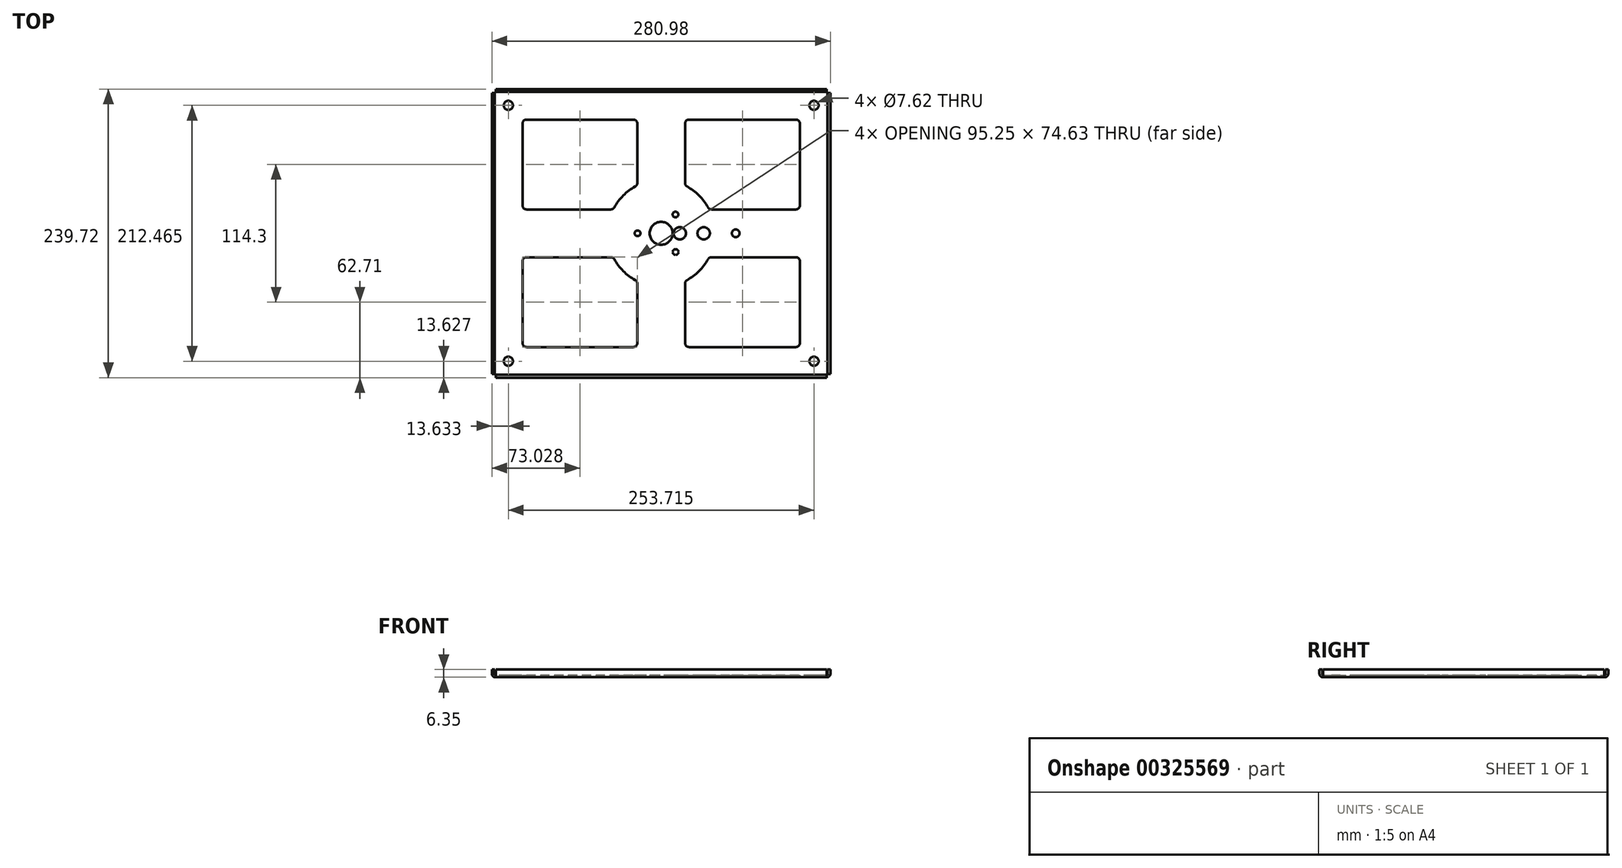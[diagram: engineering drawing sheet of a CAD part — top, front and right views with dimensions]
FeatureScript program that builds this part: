
annotation { "Feature Type Name" : "Feature", "Feature Type Description" : "" }
export const myFeature = defineFeature(function(context is Context, id is Id, definition is map)
    precondition{}
    {
        {
            var Q0;
            Q0=qCreatedBy(makeId("Top.planeOp"),FACE);
            var sketch = newSketch(context, id + "F0", { "sketchPlane" : qUnion([Q0])});
            skArc(sketch, "E0", {"start": v(-21.48, 38.92) * mm, "mid": v(-31.43, 31.43) * mm, "end": v(-38.92, 21.48) * mm});
            skLineSegment(sketch, "E1", {"start": v(-140.49, 116.69) * mm, "end": v(-140.49, -116.69) * mm});
            skLineSegment(sketch, "E2.0", {"start": v(-115.09, 91.29) * mm, "end": v(-115.09, 23.01) * mm});
            skLineSegment(sketch, "E3.0", {"start": v(-19.84, 91.29) * mm, "end": v(-19.84, 41.7) * mm});
            skLineSegment(sketch, "E4.0", {"start": v(19.84, 91.29) * mm, "end": v(19.84, 41.7) * mm});
            skLineSegment(sketch, "E5.0", {"start": v(115.09, 91.29) * mm, "end": v(115.09, 23.01) * mm});
            skLineSegment(sketch, "E6.0", {"start": v(140.49, 116.69) * mm, "end": v(140.49, -116.69) * mm});
            skLineSegment(sketch, "E7", {"start": v(-137.31, -119.86) * mm, "end": v(137.31, -119.86) * mm});
            skLineSegment(sketch, "E8.0", {"start": v(-111.91, -94.46) * mm, "end": v(-23.01, -94.46) * mm});
            skLineSegment(sketch, "E9.0", {"start": v(-111.91, -19.84) * mm, "end": v(-41.7, -19.84) * mm});
            skLineSegment(sketch, "E10.0", {"start": v(-111.91, 19.84) * mm, "end": v(-41.7, 19.84) * mm});
            skLineSegment(sketch, "E11.0", {"start": v(-111.91, 94.46) * mm, "end": v(-23.01, 94.46) * mm});
            skLineSegment(sketch, "E12.0", {"start": v(-137.31, 119.86) * mm, "end": v(137.31, 119.86) * mm});
            skLineSegment(sketch, "E13.trimOffspring", {"start": v(23.01, -94.46) * mm, "end": v(111.91, -94.46) * mm});
            skLineSegment(sketch, "E14.trimOffspring", {"start": v(-115.09, -23.01) * mm, "end": v(-115.09, -91.29) * mm});
            skLineSegment(sketch, "E15.trimOffspring", {"start": v(23.01, 94.46) * mm, "end": v(111.91, 94.46) * mm});
            skArc(sketch, "E16.trimOffspring", {"start": v(-38.92, -21.48) * mm, "mid": v(-31.43, -31.43) * mm, "end": v(-21.48, -38.92) * mm});
            skLineSegment(sketch, "E17.trimOffspring", {"start": v(41.7, 19.84) * mm, "end": v(111.91, 19.84) * mm});
            skArc(sketch, "E18.trimOffspring", {"start": v(38.92, 21.48) * mm, "mid": v(31.43, 31.43) * mm, "end": v(21.48, 38.92) * mm});
            skLineSegment(sketch, "E19.trimOffspring", {"start": v(41.7, -19.84) * mm, "end": v(111.91, -19.84) * mm});
            skLineSegment(sketch, "E20.trimOffspring", {"start": v(19.84, -41.7) * mm, "end": v(19.84, -91.29) * mm});
            skArc(sketch, "E21.trimOffspring", {"start": v(21.48, -38.92) * mm, "mid": v(31.43, -31.43) * mm, "end": v(38.92, -21.48) * mm});
            skLineSegment(sketch, "E22.trimOffspring", {"start": v(-19.84, -41.7) * mm, "end": v(-19.84, -91.29) * mm});
            skPoint(sketch, "E23.visualSharp", {"position": v(-115.09, 94.46) * mm});
            skArc(sketch, "E23.filletArc", {"start": v(-111.91, 94.46) * mm, "mid": v(-114.16, 93.53) * mm, "end": v(-115.09, 91.29) * mm});
            skPoint(sketch, "E24.visualSharp", {"position": v(-115.09, 19.84) * mm});
            skArc(sketch, "E24.filletArc", {"start": v(-115.09, 23.01) * mm, "mid": v(-114.16, 20.77) * mm, "end": v(-111.91, 19.84) * mm});
            skPoint(sketch, "E25.visualSharp", {"position": v(-39.78, 19.84) * mm});
            skArc(sketch, "E25.filletArc", {"start": v(-41.7, 19.84) * mm, "mid": v(-40.08, 20.28) * mm, "end": v(-38.92, 21.48) * mm});
            skPoint(sketch, "E26.visualSharp", {"position": v(-19.84, 39.78) * mm});
            skArc(sketch, "E26.filletArc", {"start": v(-21.48, 38.92) * mm, "mid": v(-20.28, 40.08) * mm, "end": v(-19.84, 41.7) * mm});
            skPoint(sketch, "E27.visualSharp", {"position": v(-19.84, 94.46) * mm});
            skArc(sketch, "E27.filletArc", {"start": v(-19.84, 91.29) * mm, "mid": v(-20.77, 93.53) * mm, "end": v(-23.01, 94.46) * mm});
            skPoint(sketch, "E28.visualSharp", {"position": v(19.84, 94.46) * mm});
            skArc(sketch, "E28.filletArc", {"start": v(23.01, 94.46) * mm, "mid": v(20.77, 93.53) * mm, "end": v(19.84, 91.29) * mm});
            skPoint(sketch, "E29.visualSharp", {"position": v(19.84, 39.78) * mm});
            skArc(sketch, "E29.filletArc", {"start": v(19.84, 41.7) * mm, "mid": v(20.28, 40.08) * mm, "end": v(21.48, 38.92) * mm});
            skPoint(sketch, "E30.visualSharp", {"position": v(39.78, 19.84) * mm});
            skArc(sketch, "E30.filletArc", {"start": v(38.92, 21.48) * mm, "mid": v(40.08, 20.28) * mm, "end": v(41.7, 19.84) * mm});
            skArc(sketch, "E31.filletArc", {"start": v(111.91, 19.84) * mm, "mid": v(114.16, 20.77) * mm, "end": v(115.09, 23.01) * mm});
            skPoint(sketch, "E32.visualSharp", {"position": v(115.09, 94.46) * mm});
            skArc(sketch, "E32.filletArc", {"start": v(115.09, 91.29) * mm, "mid": v(114.16, 93.53) * mm, "end": v(111.91, 94.46) * mm});
            skPoint(sketch, "E33.visualSharp", {"position": v(-39.78, -19.84) * mm});
            skArc(sketch, "E33.filletArc", {"start": v(-38.92, -21.48) * mm, "mid": v(-40.08, -20.28) * mm, "end": v(-41.7, -19.84) * mm});
            skPoint(sketch, "E34.visualSharp", {"position": v(-19.84, -39.78) * mm});
            skArc(sketch, "E34.filletArc", {"start": v(-19.84, -41.7) * mm, "mid": v(-20.28, -40.08) * mm, "end": v(-21.48, -38.92) * mm});
            skPoint(sketch, "E35.visualSharp", {"position": v(-19.84, -94.46) * mm});
            skArc(sketch, "E35.filletArc", {"start": v(-23.01, -94.46) * mm, "mid": v(-20.77, -93.53) * mm, "end": v(-19.84, -91.29) * mm});
            skPoint(sketch, "E36.visualSharp", {"position": v(-115.09, -94.46) * mm});
            skArc(sketch, "E36.filletArc", {"start": v(-115.09, -91.29) * mm, "mid": v(-114.16, -93.53) * mm, "end": v(-111.91, -94.46) * mm});
            skPoint(sketch, "E37.visualSharp", {"position": v(-115.09, -19.84) * mm});
            skArc(sketch, "E37.filletArc", {"start": v(-111.91, -19.84) * mm, "mid": v(-114.16, -20.77) * mm, "end": v(-115.09, -23.01) * mm});
            skPoint(sketch, "E38.visualSharp", {"position": v(19.84, -39.78) * mm});
            skArc(sketch, "E38.filletArc", {"start": v(21.48, -38.92) * mm, "mid": v(20.28, -40.08) * mm, "end": v(19.84, -41.7) * mm});
            skPoint(sketch, "E39.visualSharp", {"position": v(39.78, -19.84) * mm});
            skArc(sketch, "E39.filletArc", {"start": v(41.7, -19.84) * mm, "mid": v(40.08, -20.28) * mm, "end": v(38.92, -21.48) * mm});
            skPoint(sketch, "E40.visualSharp", {"position": v(19.84, -94.46) * mm});
            skArc(sketch, "E40.filletArc", {"start": v(19.84, -91.29) * mm, "mid": v(20.77, -93.53) * mm, "end": v(23.01, -94.46) * mm});
            skLineSegment(sketch, "E41", {"start": v(115.09, -91.29) * mm, "end": v(115.09, -23.01) * mm});
            skPoint(sketch, "E42.visualSharp", {"position": v(115.09, -94.46) * mm});
            skArc(sketch, "E42.filletArc", {"start": v(111.91, -94.46) * mm, "mid": v(114.16, -93.53) * mm, "end": v(115.09, -91.29) * mm});
            skPoint(sketch, "E43.visualSharp", {"position": v(115.09, -19.84) * mm});
            skArc(sketch, "E43.filletArc", {"start": v(115.09, -23.01) * mm, "mid": v(114.16, -20.77) * mm, "end": v(111.91, -19.84) * mm});
            skPoint(sketch, "E44.visualSharp", {"position": v(140.49, 119.86) * mm});
            skArc(sketch, "E44.filletArc", {"start": v(140.49, 116.69) * mm, "mid": v(139.56, 118.93) * mm, "end": v(137.31, 119.86) * mm});
            skPoint(sketch, "E45.visualSharp", {"position": v(140.49, -119.86) * mm});
            skArc(sketch, "E45.filletArc", {"start": v(137.31, -119.86) * mm, "mid": v(139.56, -118.93) * mm, "end": v(140.49, -116.69) * mm});
            skPoint(sketch, "E46.visualSharp", {"position": v(-140.49, -119.86) * mm});
            skArc(sketch, "E46.filletArc", {"start": v(-140.49, -116.69) * mm, "mid": v(-139.56, -118.93) * mm, "end": v(-137.31, -119.86) * mm});
            skPoint(sketch, "E47.visualSharp", {"position": v(-140.49, 119.86) * mm});
            skArc(sketch, "E47.filletArc", {"start": v(-137.31, 119.86) * mm, "mid": v(-139.56, 118.93) * mm, "end": v(-140.49, 116.69) * mm});
            skLineSegment(sketch, "E48", {"start": v(-139.56, -118.93) * mm, "end": v(-114.16, -93.53) * mm});
            skPoint(sketch, "E49", {"position": v(-126.86, -106.23) * mm});
            skCircle(sketch, "E50", {"center": v(-126.86, -106.23) * mm, "radius": 3.81 * mm});
            skLineSegment(sketch, "E51", {"start": v(-139.56, 118.93) * mm, "end": v(-114.16, 93.53) * mm});
            skPoint(sketch, "E52", {"position": v(-126.86, 106.23) * mm});
            skCircle(sketch, "E53", {"center": v(-126.86, 106.23) * mm, "radius": 3.81 * mm});
            skLineSegment(sketch, "E54", {"start": v(114.16, 93.53) * mm, "end": v(139.56, 118.93) * mm});
            skPoint(sketch, "E55", {"position": v(126.86, 106.23) * mm});
            skCircle(sketch, "E56", {"center": v(126.86, 106.23) * mm, "radius": 3.81 * mm});
            skLineSegment(sketch, "E57", {"start": v(114.16, -93.53) * mm, "end": v(139.56, -118.93) * mm});
            skPoint(sketch, "E58", {"position": v(126.86, -106.23) * mm});
            skCircle(sketch, "E59", {"center": v(126.86, -106.23) * mm, "radius": 3.81 * mm});
            skCircle(sketch, "E60", {"center": v(15.47, 0) * mm, "radius": 5.16 * mm});
            skLineSegment(sketch, "E61", {"start": v(0, 0) * mm, "end": v(-174.23, 0) * mm, "construction": true});
            skLineSegment(sketch, "E62", {"start": v(-174.23, 0) * mm, "end": v(-174.23, 0) * mm});
            skLineSegment(sketch, "E63", {"start": v(0, 0) * mm, "end": v(180.46, 0) * mm, "construction": true});
            skLineSegment(sketch, "E64", {"start": v(0, -149.74) * mm, "end": v(0, 151.2) * mm, "construction": true});
            skCircle(sketch, "E65", {"center": v(0, 0) * mm, "radius": 9.53 * mm});
            skCircle(sketch, "E66", {"center": v(35.31, 0) * mm, "radius": 5.16 * mm});
            skCircle(sketch, "E67", {"center": v(-19.56, 0) * mm, "radius": 2.38 * mm});
            skPoint(sketch, "E68", {"position": v(-31.43, 31.43) * mm});
            skPoint(sketch, "E69", {"position": v(-31.43, -31.43) * mm});
            skCircle(sketch, "E70", {"center": v(0, 0) * mm, "radius": 17.22 * mm});
            skCircle(sketch, "E71", {"center": v(11.9, 15.59) * mm, "radius": 2.39 * mm});
            skCircle(sketch, "E72", {"center": v(12, -15.56) * mm, "radius": 2.39 * mm});
            skLineSegment(sketch, "E73", {"start": v(9.53, 0) * mm, "end": v(9.53, 25.1) * mm, "construction": true});
            skLineSegment(sketch, "E74", {"start": v(9.53, 0) * mm, "end": v(9.53, -24.17) * mm, "construction": true});
            skCircle(sketch, "E75", {"center": v(61.91, 0) * mm, "radius": 3.18 * mm});
            skSolve(sketch);
        }
        {
            var Q0;
            Q0=makeQuery(id+"F0.imprint","IMPRINT",FACE,{"disambiguationData":[TD([[makeQuery(id+"F0.imprint","IMPRINT",EDGE,{"derivedFrom":sQuery(id+"F0.wireOp",EDGE,"E0")}),1.0]])]});
            var Q1;
            {var subQ14=sQuery(id+"F0.wireOp",EDGE,"E5.0");Q1=makeQuery(id+"F0.imprint","IMPRINT",FACE,{"disambiguationData":[TD([[makeQuery(id+"F0.imprint","IMPRINT",EDGE,{"derivedFrom":subQ14}),1.0]])]});}
            var Q2;
            Q2=makeQuery(id+"F0.imprint","IMPRINT",FACE,{"disambiguationData":[TD([[makeQuery(id+"F0.imprint","IMPRINT",EDGE,{"derivedFrom":sQuery(id+"F0.wireOp",EDGE,"E65")}),-1.0]])]});
            extrude(context, id + "F1", {"entities" : qUnion([Q0, Q1, Q2]), "depth" : 1.59 * mm});
        }
        {
            var Q0;
            Q0=qCreatedBy(makeId("Top.planeOp"),FACE);
            var sketch = newSketch(context, id + "F2", { "sketchPlane" : qUnion([Q0])});
            skLineSegment(sketch, "E76", {"start": v(-138.1, 116.68) * mm, "end": v(-138.1, -116.68) * mm});
            skLineSegment(sketch, "E77.0", {"start": v(-140.49, 116.68) * mm, "end": v(-140.49, -116.68) * mm});
            skLineSegment(sketch, "E78", {"start": v(138.1, 116.68) * mm, "end": v(138.1, -116.68) * mm});
            skLineSegment(sketch, "E79.0", {"start": v(140.49, 116.68) * mm, "end": v(140.49, -116.68) * mm});
            skLineSegment(sketch, "E80", {"start": v(-137.33, -117.48) * mm, "end": v(137.3, -117.48) * mm});
            skLineSegment(sketch, "E81.0", {"start": v(-137.33, 117.48) * mm, "end": v(137.3, 117.48) * mm});
            skLineSegment(sketch, "E82.0", {"start": v(-137.33, -119.86) * mm, "end": v(137.3, -119.86) * mm});
            skLineSegment(sketch, "E83", {"start": v(-137.33, 119.86) * mm, "end": v(-137.33, 117.48) * mm});
            skLineSegment(sketch, "E84", {"start": v(137.3, 119.86) * mm, "end": v(137.3, 117.48) * mm});
            skLineSegment(sketch, "E85", {"start": v(-140.49, 116.68) * mm, "end": v(-138.1, 116.68) * mm});
            skLineSegment(sketch, "E86", {"start": v(-140.49, -116.68) * mm, "end": v(-138.1, -116.68) * mm});
            skLineSegment(sketch, "E87.trimOffspring", {"start": v(-137.33, 119.86) * mm, "end": v(137.3, 119.86) * mm});
            skLineSegment(sketch, "E88.trimOffspring", {"start": v(137.3, -117.48) * mm, "end": v(137.3, -119.86) * mm});
            skLineSegment(sketch, "E89.trimOffspring", {"start": v(138.1, 116.68) * mm, "end": v(140.49, 116.68) * mm});
            skLineSegment(sketch, "E90.trimOffspring", {"start": v(-137.33, -117.48) * mm, "end": v(-137.33, -119.86) * mm});
            skLineSegment(sketch, "E91.trimOffspring", {"start": v(138.1, -116.68) * mm, "end": v(140.49, -116.68) * mm});
            skSolve(sketch);
        }
        {
            var Q0;
            Q0=makeQuery(id+"F2.imprint","IMPRINT",FACE,{"disambiguationData":[TD([[makeQuery(id+"F2.imprint","IMPRINT",EDGE,{"derivedFrom":sQuery(id+"F2.wireOp",EDGE,"E81.0")}),1.0]])]});
            var Q1;
            Q1=makeQuery(id+"F2.imprint","IMPRINT",FACE,{"disambiguationData":[TD([[makeQuery(id+"F2.imprint","IMPRINT",EDGE,{"derivedFrom":sQuery(id+"F2.wireOp",EDGE,"E78")}),1.0]])]});
            var Q2;
            Q2=makeQuery(id+"F2.imprint","IMPRINT",FACE,{"disambiguationData":[TD([[makeQuery(id+"F2.imprint","IMPRINT",EDGE,{"derivedFrom":sQuery(id+"F2.wireOp",EDGE,"E80")}),-1.0]])]});
            var Q3;
            Q3=makeQuery(id+"F2.imprint","IMPRINT",FACE,{"disambiguationData":[TD([[makeQuery(id+"F2.imprint","IMPRINT",EDGE,{"derivedFrom":sQuery(id+"F2.wireOp",EDGE,"E76")}),-1.0]])]});
            extrude(context, id + "F3", {"entities" : qUnion([Q0, Q1, Q2, Q3]), "operationType" : NewBodyOperationType.ADD, "depth" : 6.35 * mm});
        }
        {
            var Q0;
            Q0=makeQuery(id+"F3.boolean.opBoolean","INTERSECT",EDGE,{"derivedFrom":[makeQuery(id+"F1.opExtrude","CAP_FACE",FACE,{"disambiguationData":[OSD([sQuery(id+"F0.wireOp",EDGE,"E0"),sQuery(id+"F0.wireOp",EDGE,"E1"),sQuery(id+"F0.wireOp",EDGE,"E2.0"),sQuery(id+"F0.wireOp",EDGE,"E3.0"),sQuery(id+"F0.wireOp",EDGE,"E4.0"),sQuery(id+"F0.wireOp",EDGE,"E5.0"),sQuery(id+"F0.wireOp",EDGE,"E6.0"),sQuery(id+"F0.wireOp",EDGE,"E7"),sQuery(id+"F0.wireOp",EDGE,"E8.0"),sQuery(id+"F0.wireOp",EDGE,"E9.0"),sQuery(id+"F0.wireOp",EDGE,"E10.0"),sQuery(id+"F0.wireOp",EDGE,"E11.0"),sQuery(id+"F0.wireOp",EDGE,"E12.0"),sQuery(id+"F0.wireOp",EDGE,"E13.trimOffspring"),sQuery(id+"F0.wireOp",EDGE,"E14.trimOffspring"),sQuery(id+"F0.wireOp",EDGE,"E15.trimOffspring"),sQuery(id+"F0.wireOp",EDGE,"E16.trimOffspring"),sQuery(id+"F0.wireOp",EDGE,"E17.trimOffspring"),sQuery(id+"F0.wireOp",EDGE,"E18.trimOffspring"),sQuery(id+"F0.wireOp",EDGE,"E19.trimOffspring"),sQuery(id+"F0.wireOp",EDGE,"E20.trimOffspring"),sQuery(id+"F0.wireOp",EDGE,"E21.trimOffspring"),sQuery(id+"F0.wireOp",EDGE,"E22.trimOffspring"),sQuery(id+"F0.wireOp",EDGE,"E23.filletArc"),sQuery(id+"F0.wireOp",EDGE,"E24.filletArc"),sQuery(id+"F0.wireOp",EDGE,"E25.filletArc"),sQuery(id+"F0.wireOp",EDGE,"E26.filletArc"),sQuery(id+"F0.wireOp",EDGE,"E27.filletArc"),sQuery(id+"F0.wireOp",EDGE,"E28.filletArc"),sQuery(id+"F0.wireOp",EDGE,"E29.filletArc"),sQuery(id+"F0.wireOp",EDGE,"E30.filletArc"),sQuery(id+"F0.wireOp",EDGE,"E31.filletArc"),sQuery(id+"F0.wireOp",EDGE,"E32.filletArc"),sQuery(id+"F0.wireOp",EDGE,"E33.filletArc"),sQuery(id+"F0.wireOp",EDGE,"E34.filletArc"),sQuery(id+"F0.wireOp",EDGE,"E35.filletArc"),sQuery(id+"F0.wireOp",EDGE,"E36.filletArc"),sQuery(id+"F0.wireOp",EDGE,"E37.filletArc"),sQuery(id+"F0.wireOp",EDGE,"E38.filletArc"),sQuery(id+"F0.wireOp",EDGE,"E39.filletArc"),sQuery(id+"F0.wireOp",EDGE,"E40.filletArc"),sQuery(id+"F0.wireOp",EDGE,"E41"),sQuery(id+"F0.wireOp",EDGE,"E42.filletArc"),sQuery(id+"F0.wireOp",EDGE,"E43.filletArc"),sQuery(id+"F0.wireOp",EDGE,"E44.filletArc"),sQuery(id+"F0.wireOp",EDGE,"E45.filletArc"),sQuery(id+"F0.wireOp",EDGE,"E46.filletArc"),sQuery(id+"F0.wireOp",EDGE,"E47.filletArc"),sQuery(id+"F0.wireOp",EDGE,"E50"),sQuery(id+"F0.wireOp",EDGE,"E53"),sQuery(id+"F0.wireOp",EDGE,"E56"),sQuery(id+"F0.wireOp",EDGE,"E59"),sQuery(id+"F0.wireOp",EDGE,"E60"),sQuery(id+"F0.wireOp",EDGE,"4c565e8e-d8a4-4b50-a715-5eb734d49097")])],"isStart":false}),makeQuery(id+"F3.opExtrude","SWEPT_FACE",FACE,{"disambiguationData":[OSD([sQuery(id+"F2.wireOp",EDGE,"E81.0")])]})]});
            var Q1;
            Q1=makeQuery(id+"F3.boolean.opBoolean","INTERSECT",EDGE,{"derivedFrom":[makeQuery(id+"F1.opExtrude","CAP_FACE",FACE,{"disambiguationData":[OSD([sQuery(id+"F0.wireOp",EDGE,"E0"),sQuery(id+"F0.wireOp",EDGE,"E1"),sQuery(id+"F0.wireOp",EDGE,"E2.0"),sQuery(id+"F0.wireOp",EDGE,"E3.0"),sQuery(id+"F0.wireOp",EDGE,"E4.0"),sQuery(id+"F0.wireOp",EDGE,"E5.0"),sQuery(id+"F0.wireOp",EDGE,"E6.0"),sQuery(id+"F0.wireOp",EDGE,"E7"),sQuery(id+"F0.wireOp",EDGE,"E8.0"),sQuery(id+"F0.wireOp",EDGE,"E9.0"),sQuery(id+"F0.wireOp",EDGE,"E10.0"),sQuery(id+"F0.wireOp",EDGE,"E11.0"),sQuery(id+"F0.wireOp",EDGE,"E12.0"),sQuery(id+"F0.wireOp",EDGE,"E13.trimOffspring"),sQuery(id+"F0.wireOp",EDGE,"E14.trimOffspring"),sQuery(id+"F0.wireOp",EDGE,"E15.trimOffspring"),sQuery(id+"F0.wireOp",EDGE,"E16.trimOffspring"),sQuery(id+"F0.wireOp",EDGE,"E17.trimOffspring"),sQuery(id+"F0.wireOp",EDGE,"E18.trimOffspring"),sQuery(id+"F0.wireOp",EDGE,"E19.trimOffspring"),sQuery(id+"F0.wireOp",EDGE,"E20.trimOffspring"),sQuery(id+"F0.wireOp",EDGE,"E21.trimOffspring"),sQuery(id+"F0.wireOp",EDGE,"E22.trimOffspring"),sQuery(id+"F0.wireOp",EDGE,"E23.filletArc"),sQuery(id+"F0.wireOp",EDGE,"E24.filletArc"),sQuery(id+"F0.wireOp",EDGE,"E25.filletArc"),sQuery(id+"F0.wireOp",EDGE,"E26.filletArc"),sQuery(id+"F0.wireOp",EDGE,"E27.filletArc"),sQuery(id+"F0.wireOp",EDGE,"E28.filletArc"),sQuery(id+"F0.wireOp",EDGE,"E29.filletArc"),sQuery(id+"F0.wireOp",EDGE,"E30.filletArc"),sQuery(id+"F0.wireOp",EDGE,"E31.filletArc"),sQuery(id+"F0.wireOp",EDGE,"E32.filletArc"),sQuery(id+"F0.wireOp",EDGE,"E33.filletArc"),sQuery(id+"F0.wireOp",EDGE,"E34.filletArc"),sQuery(id+"F0.wireOp",EDGE,"E35.filletArc"),sQuery(id+"F0.wireOp",EDGE,"E36.filletArc"),sQuery(id+"F0.wireOp",EDGE,"E37.filletArc"),sQuery(id+"F0.wireOp",EDGE,"E38.filletArc"),sQuery(id+"F0.wireOp",EDGE,"E39.filletArc"),sQuery(id+"F0.wireOp",EDGE,"E40.filletArc"),sQuery(id+"F0.wireOp",EDGE,"E41"),sQuery(id+"F0.wireOp",EDGE,"E42.filletArc"),sQuery(id+"F0.wireOp",EDGE,"E43.filletArc"),sQuery(id+"F0.wireOp",EDGE,"E44.filletArc"),sQuery(id+"F0.wireOp",EDGE,"E45.filletArc"),sQuery(id+"F0.wireOp",EDGE,"E46.filletArc"),sQuery(id+"F0.wireOp",EDGE,"E47.filletArc"),sQuery(id+"F0.wireOp",EDGE,"E50"),sQuery(id+"F0.wireOp",EDGE,"E53"),sQuery(id+"F0.wireOp",EDGE,"E56"),sQuery(id+"F0.wireOp",EDGE,"E59"),sQuery(id+"F0.wireOp",EDGE,"E60"),sQuery(id+"F0.wireOp",EDGE,"4c565e8e-d8a4-4b50-a715-5eb734d49097")])],"isStart":false}),makeQuery(id+"F3.opExtrude","SWEPT_FACE",FACE,{"disambiguationData":[OSD([sQuery(id+"F2.wireOp",EDGE,"E78")])]})]});
            var Q2;
            Q2=makeQuery(id+"F3.boolean.opBoolean","INTERSECT",EDGE,{"derivedFrom":[makeQuery(id+"F1.opExtrude","CAP_FACE",FACE,{"disambiguationData":[OSD([sQuery(id+"F0.wireOp",EDGE,"E0"),sQuery(id+"F0.wireOp",EDGE,"E1"),sQuery(id+"F0.wireOp",EDGE,"E2.0"),sQuery(id+"F0.wireOp",EDGE,"E3.0"),sQuery(id+"F0.wireOp",EDGE,"E4.0"),sQuery(id+"F0.wireOp",EDGE,"E5.0"),sQuery(id+"F0.wireOp",EDGE,"E6.0"),sQuery(id+"F0.wireOp",EDGE,"E7"),sQuery(id+"F0.wireOp",EDGE,"E8.0"),sQuery(id+"F0.wireOp",EDGE,"E9.0"),sQuery(id+"F0.wireOp",EDGE,"E10.0"),sQuery(id+"F0.wireOp",EDGE,"E11.0"),sQuery(id+"F0.wireOp",EDGE,"E12.0"),sQuery(id+"F0.wireOp",EDGE,"E13.trimOffspring"),sQuery(id+"F0.wireOp",EDGE,"E14.trimOffspring"),sQuery(id+"F0.wireOp",EDGE,"E15.trimOffspring"),sQuery(id+"F0.wireOp",EDGE,"E16.trimOffspring"),sQuery(id+"F0.wireOp",EDGE,"E17.trimOffspring"),sQuery(id+"F0.wireOp",EDGE,"E18.trimOffspring"),sQuery(id+"F0.wireOp",EDGE,"E19.trimOffspring"),sQuery(id+"F0.wireOp",EDGE,"E20.trimOffspring"),sQuery(id+"F0.wireOp",EDGE,"E21.trimOffspring"),sQuery(id+"F0.wireOp",EDGE,"E22.trimOffspring"),sQuery(id+"F0.wireOp",EDGE,"E23.filletArc"),sQuery(id+"F0.wireOp",EDGE,"E24.filletArc"),sQuery(id+"F0.wireOp",EDGE,"E25.filletArc"),sQuery(id+"F0.wireOp",EDGE,"E26.filletArc"),sQuery(id+"F0.wireOp",EDGE,"E27.filletArc"),sQuery(id+"F0.wireOp",EDGE,"E28.filletArc"),sQuery(id+"F0.wireOp",EDGE,"E29.filletArc"),sQuery(id+"F0.wireOp",EDGE,"E30.filletArc"),sQuery(id+"F0.wireOp",EDGE,"E31.filletArc"),sQuery(id+"F0.wireOp",EDGE,"E32.filletArc"),sQuery(id+"F0.wireOp",EDGE,"E33.filletArc"),sQuery(id+"F0.wireOp",EDGE,"E34.filletArc"),sQuery(id+"F0.wireOp",EDGE,"E35.filletArc"),sQuery(id+"F0.wireOp",EDGE,"E36.filletArc"),sQuery(id+"F0.wireOp",EDGE,"E37.filletArc"),sQuery(id+"F0.wireOp",EDGE,"E38.filletArc"),sQuery(id+"F0.wireOp",EDGE,"E39.filletArc"),sQuery(id+"F0.wireOp",EDGE,"E40.filletArc"),sQuery(id+"F0.wireOp",EDGE,"E41"),sQuery(id+"F0.wireOp",EDGE,"E42.filletArc"),sQuery(id+"F0.wireOp",EDGE,"E43.filletArc"),sQuery(id+"F0.wireOp",EDGE,"E44.filletArc"),sQuery(id+"F0.wireOp",EDGE,"E45.filletArc"),sQuery(id+"F0.wireOp",EDGE,"E46.filletArc"),sQuery(id+"F0.wireOp",EDGE,"E47.filletArc"),sQuery(id+"F0.wireOp",EDGE,"E50"),sQuery(id+"F0.wireOp",EDGE,"E53"),sQuery(id+"F0.wireOp",EDGE,"E56"),sQuery(id+"F0.wireOp",EDGE,"E59"),sQuery(id+"F0.wireOp",EDGE,"E60"),sQuery(id+"F0.wireOp",EDGE,"4c565e8e-d8a4-4b50-a715-5eb734d49097")])],"isStart":false}),makeQuery(id+"F3.opExtrude","SWEPT_FACE",FACE,{"disambiguationData":[OSD([sQuery(id+"F2.wireOp",EDGE,"E80")])]})]});
            var Q3;
            Q3=makeQuery(id+"F3.boolean.opBoolean","INTERSECT",EDGE,{"derivedFrom":[makeQuery(id+"F1.opExtrude","CAP_FACE",FACE,{"disambiguationData":[OSD([sQuery(id+"F0.wireOp",EDGE,"E0"),sQuery(id+"F0.wireOp",EDGE,"E1"),sQuery(id+"F0.wireOp",EDGE,"E2.0"),sQuery(id+"F0.wireOp",EDGE,"E3.0"),sQuery(id+"F0.wireOp",EDGE,"E4.0"),sQuery(id+"F0.wireOp",EDGE,"E5.0"),sQuery(id+"F0.wireOp",EDGE,"E6.0"),sQuery(id+"F0.wireOp",EDGE,"E7"),sQuery(id+"F0.wireOp",EDGE,"E8.0"),sQuery(id+"F0.wireOp",EDGE,"E9.0"),sQuery(id+"F0.wireOp",EDGE,"E10.0"),sQuery(id+"F0.wireOp",EDGE,"E11.0"),sQuery(id+"F0.wireOp",EDGE,"E12.0"),sQuery(id+"F0.wireOp",EDGE,"E13.trimOffspring"),sQuery(id+"F0.wireOp",EDGE,"E14.trimOffspring"),sQuery(id+"F0.wireOp",EDGE,"E15.trimOffspring"),sQuery(id+"F0.wireOp",EDGE,"E16.trimOffspring"),sQuery(id+"F0.wireOp",EDGE,"E17.trimOffspring"),sQuery(id+"F0.wireOp",EDGE,"E18.trimOffspring"),sQuery(id+"F0.wireOp",EDGE,"E19.trimOffspring"),sQuery(id+"F0.wireOp",EDGE,"E20.trimOffspring"),sQuery(id+"F0.wireOp",EDGE,"E21.trimOffspring"),sQuery(id+"F0.wireOp",EDGE,"E22.trimOffspring"),sQuery(id+"F0.wireOp",EDGE,"E23.filletArc"),sQuery(id+"F0.wireOp",EDGE,"E24.filletArc"),sQuery(id+"F0.wireOp",EDGE,"E25.filletArc"),sQuery(id+"F0.wireOp",EDGE,"E26.filletArc"),sQuery(id+"F0.wireOp",EDGE,"E27.filletArc"),sQuery(id+"F0.wireOp",EDGE,"E28.filletArc"),sQuery(id+"F0.wireOp",EDGE,"E29.filletArc"),sQuery(id+"F0.wireOp",EDGE,"E30.filletArc"),sQuery(id+"F0.wireOp",EDGE,"E31.filletArc"),sQuery(id+"F0.wireOp",EDGE,"E32.filletArc"),sQuery(id+"F0.wireOp",EDGE,"E33.filletArc"),sQuery(id+"F0.wireOp",EDGE,"E34.filletArc"),sQuery(id+"F0.wireOp",EDGE,"E35.filletArc"),sQuery(id+"F0.wireOp",EDGE,"E36.filletArc"),sQuery(id+"F0.wireOp",EDGE,"E37.filletArc"),sQuery(id+"F0.wireOp",EDGE,"E38.filletArc"),sQuery(id+"F0.wireOp",EDGE,"E39.filletArc"),sQuery(id+"F0.wireOp",EDGE,"E40.filletArc"),sQuery(id+"F0.wireOp",EDGE,"E41"),sQuery(id+"F0.wireOp",EDGE,"E42.filletArc"),sQuery(id+"F0.wireOp",EDGE,"E43.filletArc"),sQuery(id+"F0.wireOp",EDGE,"E44.filletArc"),sQuery(id+"F0.wireOp",EDGE,"E45.filletArc"),sQuery(id+"F0.wireOp",EDGE,"E46.filletArc"),sQuery(id+"F0.wireOp",EDGE,"E47.filletArc"),sQuery(id+"F0.wireOp",EDGE,"E50"),sQuery(id+"F0.wireOp",EDGE,"E53"),sQuery(id+"F0.wireOp",EDGE,"E56"),sQuery(id+"F0.wireOp",EDGE,"E59"),sQuery(id+"F0.wireOp",EDGE,"E60"),sQuery(id+"F0.wireOp",EDGE,"4c565e8e-d8a4-4b50-a715-5eb734d49097")])],"isStart":false}),makeQuery(id+"F3.opExtrude","SWEPT_FACE",FACE,{"disambiguationData":[OSD([sQuery(id+"F2.wireOp",EDGE,"E76")])]})]});
            fillet(context, id + "F4", {"entities" : qUnion([Q0, Q1, Q2, Q3]), "radius" : 0.76 * mm, "tangentPropagation" : true, "allowEdgeOverflow" : false});
        }
        {
            var Q0;
            Q0=qCreatedBy(makeId("Top.planeOp"),FACE);
            var sketch = newSketch(context, id + "F5", { "sketchPlane" : qUnion([Q0])});
            skLineSegment(sketch, "E92.bottom", {"start": v(-141.66, 120.91) * mm, "end": v(-137.32, 120.91) * mm});
            skLineSegment(sketch, "E92.top", {"start": v(-141.66, 116.68) * mm, "end": v(-137.32, 116.68) * mm});
            skLineSegment(sketch, "E92.left", {"start": v(-141.66, 120.91) * mm, "end": v(-141.66, 116.68) * mm});
            skLineSegment(sketch, "E92.right", {"start": v(-137.32, 120.91) * mm, "end": v(-137.32, 116.68) * mm});
            skLineSegment(sketch, "E93.bottom", {"start": v(145, 124.29) * mm, "end": v(137.31, 124.29) * mm});
            skLineSegment(sketch, "E93.top", {"start": v(145, 116.68) * mm, "end": v(137.31, 116.68) * mm});
            skLineSegment(sketch, "E93.left", {"start": v(145, 124.29) * mm, "end": v(145, 116.68) * mm});
            skLineSegment(sketch, "E93.right", {"start": v(137.31, 124.29) * mm, "end": v(137.31, 116.68) * mm});
            skLineSegment(sketch, "E94.bottom", {"start": v(145, -123.46) * mm, "end": v(137.31, -123.46) * mm});
            skLineSegment(sketch, "E94.top", {"start": v(145, -116.68) * mm, "end": v(137.31, -116.68) * mm});
            skLineSegment(sketch, "E94.left", {"start": v(145, -123.46) * mm, "end": v(145, -116.68) * mm});
            skLineSegment(sketch, "E94.right", {"start": v(137.31, -123.46) * mm, "end": v(137.31, -116.68) * mm});
            skLineSegment(sketch, "E95.bottom", {"start": v(-145.82, -123.08) * mm, "end": v(-137.33, -123.08) * mm});
            skLineSegment(sketch, "E95.top", {"start": v(-145.82, -116.68) * mm, "end": v(-137.33, -116.68) * mm});
            skLineSegment(sketch, "E95.left", {"start": v(-145.82, -123.08) * mm, "end": v(-145.82, -116.68) * mm});
            skLineSegment(sketch, "E95.right", {"start": v(-137.33, -123.08) * mm, "end": v(-137.33, -116.68) * mm});
            skSolve(sketch);
        }
        {
            var Q0;
            Q0=makeQuery(id+"F5.imprint","IMPRINT",FACE,{"disambiguationData":[TD([[makeQuery(id+"F5.imprint","IMPRINT",EDGE,{"derivedFrom":sQuery(id+"F5.wireOp",EDGE,"E93.bottom")}),1.0]])]});
            var Q1;
            Q1=makeQuery(id+"F5.imprint","IMPRINT",FACE,{"disambiguationData":[TD([[makeQuery(id+"F5.imprint","IMPRINT",EDGE,{"derivedFrom":sQuery(id+"F5.wireOp",EDGE,"E92.bottom")}),-1.0]])]});
            var Q2;
            Q2=makeQuery(id+"F5.imprint","IMPRINT",FACE,{"disambiguationData":[TD([[makeQuery(id+"F5.imprint","IMPRINT",EDGE,{"derivedFrom":sQuery(id+"F5.wireOp",EDGE,"E95.bottom")}),1.0]])]});
            var Q3;
            Q3=makeQuery(id+"F5.imprint","IMPRINT",FACE,{"disambiguationData":[TD([[makeQuery(id+"F5.imprint","IMPRINT",EDGE,{"derivedFrom":sQuery(id+"F5.wireOp",EDGE,"E94.bottom")}),-1.0]])]});
            extrude(context, id + "F6", {"entities" : qUnion([Q0, Q1, Q2, Q3]), "operationType" : NewBodyOperationType.REMOVE, "endBound" : BoundingType.SYMMETRIC, "depth" : 25.4 * mm});
        }
        {
            var Q0;
            Q0=makeQuery(id+"F1.opExtrude","CAP_EDGE",EDGE,{"disambiguationData":[OSD([sQuery(id+"F0.wireOp",EDGE,"E12.0")])],"isStart":true});
            var Q1;
            Q1=makeQuery(id+"F1.opExtrude","CAP_EDGE",EDGE,{"disambiguationData":[OSD([sQuery(id+"F0.wireOp",EDGE,"E1")])],"isStart":true});
            var Q2;
            Q2=makeQuery(id+"F1.opExtrude","CAP_EDGE",EDGE,{"disambiguationData":[OSD([sQuery(id+"F0.wireOp",EDGE,"E6.0")])],"isStart":true});
            var Q3;
            Q3=makeQuery(id+"F1.opExtrude","CAP_EDGE",EDGE,{"disambiguationData":[OSD([sQuery(id+"F0.wireOp",EDGE,"E7")])],"isStart":true});
            fillet(context, id + "F7", {"entities" : qUnion([Q0, Q1, Q2, Q3]), "radius" : 2.8 * mm, "tangentPropagation" : true, "allowEdgeOverflow" : false});
        }
    });
